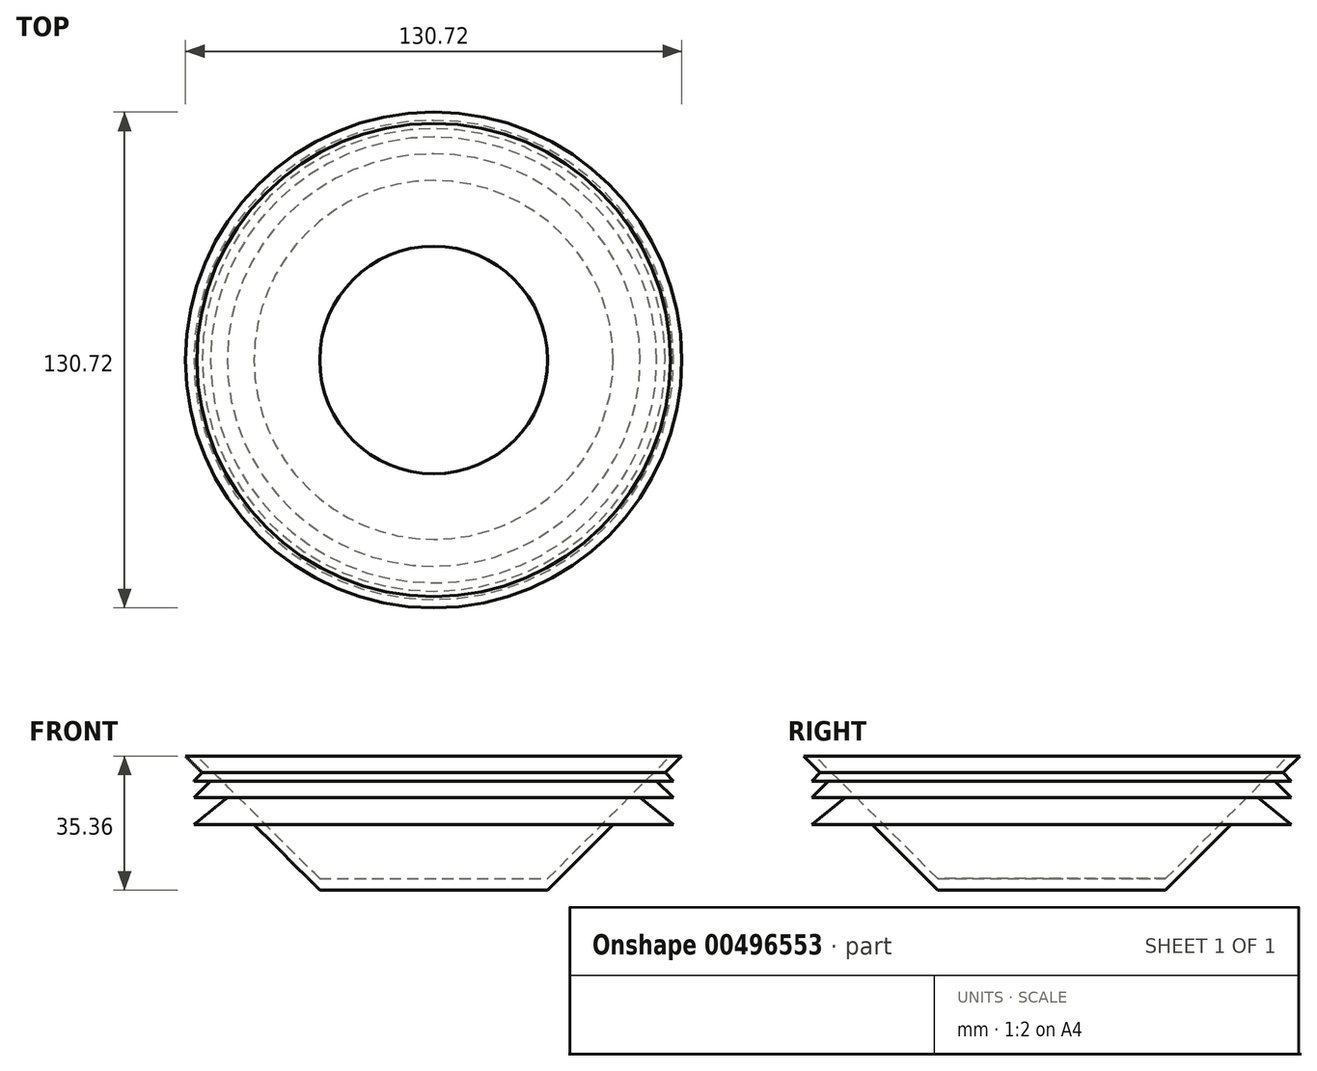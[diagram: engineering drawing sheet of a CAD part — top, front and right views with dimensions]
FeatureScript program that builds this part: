
annotation { "Feature Type Name" : "Feature", "Feature Type Description" : "" }
export const myFeature = defineFeature(function(context is Context, id is Id, definition is map)
    precondition{}
    {
        {
            var Q0;
            Q0=qCreatedBy(makeId("Front.planeOp"),FACE);
            var sketch = newSketch(context, id + "F0", { "sketchPlane" : qUnion([Q0])});
            skLineSegment(sketch, "E0", {"start": v(0, 0) * mm, "end": v(30, 0) * mm});
            skLineSegment(sketch, "E1", {"start": v(30, 0) * mm, "end": v(65.36, 35.36) * mm});
            skLineSegment(sketch, "E2", {"start": v(65.36, 35.36) * mm, "end": v(62.36, 35.36) * mm});
            skLineSegment(sketch, "E3", {"start": v(62.36, 35.36) * mm, "end": v(30, 3) * mm});
            skLineSegment(sketch, "E4", {"start": v(30, 3) * mm, "end": v(0, 3) * mm});
            skLineSegment(sketch, "E5", {"start": v(0, 3) * mm, "end": v(0, 0) * mm});
            skLineSegment(sketch, "E6", {"start": v(0, 0) * mm, "end": v(0, 35.36) * mm});
            skLineSegment(sketch, "E7", {"start": v(60.95, 30.95) * mm, "end": v(63.15, 28.76) * mm});
            skLineSegment(sketch, "E8", {"start": v(63.15, 28.76) * mm, "end": v(58.76, 28.76) * mm});
            skLineSegment(sketch, "E9", {"start": v(58.76, 28.76) * mm, "end": v(63.15, 24.36) * mm});
            skLineSegment(sketch, "E10", {"start": v(63.15, 24.36) * mm, "end": v(54.36, 24.36) * mm});
            skLineSegment(sketch, "E11", {"start": v(54.36, 24.36) * mm, "end": v(63.15, 17.3) * mm});
            skLineSegment(sketch, "E12", {"start": v(63.15, 17.3) * mm, "end": v(47.3, 17.3) * mm});
            skSolve(sketch);
        }
        {
            var Q0;
            {var subQ0=sQuery(id+"F0.wireOp",EDGE,"E0");Q0=makeQuery(id+"F0.imprint","IMPRINT",FACE,{"disambiguationData":[TD([[makeQuery(id+"F0.imprint","IMPRINT",EDGE,{"derivedFrom":subQ0}),1.0]])]});}
            var Q1;
            {var subQ0=sQuery(id+"F0.wireOp",EDGE,"E11");Q1=makeQuery(id+"F0.imprint","IMPRINT",FACE,{"disambiguationData":[TD([[makeQuery(id+"F0.imprint","IMPRINT",EDGE,{"derivedFrom":subQ0}),-1.0]])]});}
            var Q2;
            {var subQ0=sQuery(id+"F0.wireOp",EDGE,"E9");Q2=makeQuery(id+"F0.imprint","IMPRINT",FACE,{"disambiguationData":[TD([[makeQuery(id+"F0.imprint","IMPRINT",EDGE,{"derivedFrom":subQ0}),-1.0]])]});}
            var Q3;
            {var subQ0=sQuery(id+"F0.wireOp",EDGE,"E7");Q3=makeQuery(id+"F0.imprint","IMPRINT",FACE,{"disambiguationData":[TD([[makeQuery(id+"F0.imprint","IMPRINT",EDGE,{"derivedFrom":subQ0}),-1.0]])]});}
            var Q4;
            Q4=sQuery(id+"F0.wireOp",EDGE,"E6");
            revolve(context, id + "F1", {"entities" : qUnion([Q0, Q1, Q2, Q3]), "axis" : qUnion([Q4]), "revolveType" : RevolveType.FULL});
        }
    });
